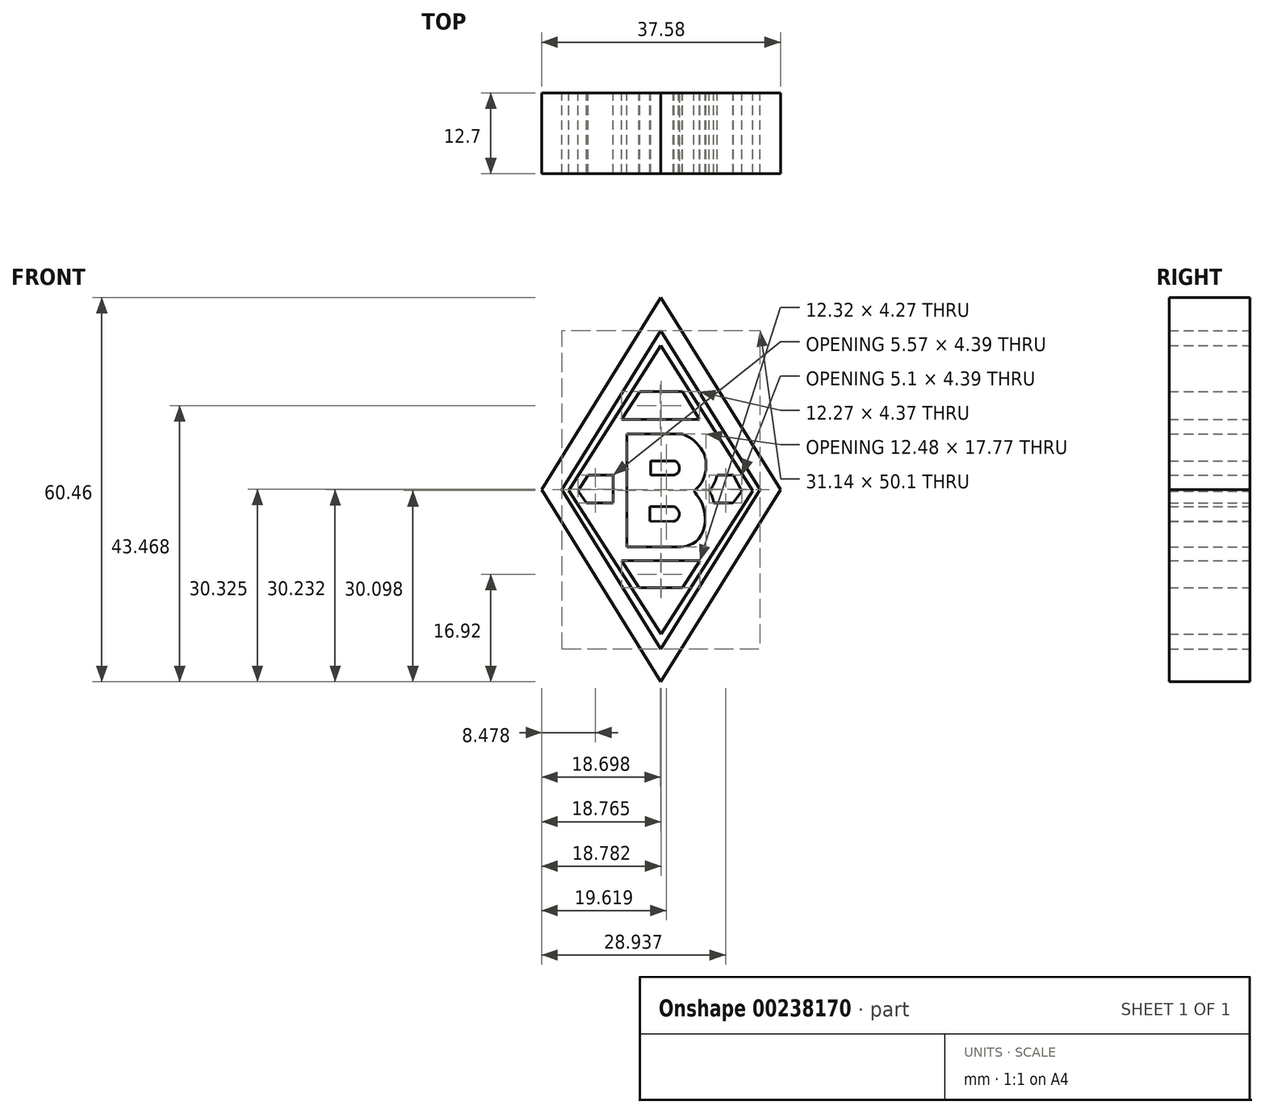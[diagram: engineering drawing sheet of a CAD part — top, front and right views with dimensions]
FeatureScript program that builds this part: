
annotation { "Feature Type Name" : "Feature", "Feature Type Description" : "" }
export const myFeature = defineFeature(function(context is Context, id is Id, definition is map)
    precondition{}
    {
        {
            var Q0;
            Q0=qCreatedBy(makeId("Front.planeOp"),FACE);
            var sketch = newSketch(context, id + "F0", { "sketchPlane" : qUnion([Q0])});
            skLineSegment(sketch, "E0", {"start": v(36.95, 66.96) * mm, "end": v(18.2, 36.72) * mm});
            skPoint(sketch, "E0.startSnap0", {"position": v(36.95, 69.13) * mm});
            skPoint(sketch, "E0.endSnap0", {"position": v(17, 36.72) * mm});
            skLineSegment(sketch, "E1", {"start": v(18.2, 36.72) * mm, "end": v(36.95, 6.5) * mm});
            skPoint(sketch, "E1.endSnap0", {"position": v(36.95, 4.31) * mm});
            skLineSegment(sketch, "E2", {"start": v(36.95, 6.5) * mm, "end": v(55.8, 36.72) * mm});
            skLineSegment(sketch, "E3", {"start": v(55.8, 36.72) * mm, "end": v(36.95, 66.96) * mm});
            skLineSegment(sketch, "E4", {"start": v(21.42, 36.72) * mm, "end": v(36.95, 61.78) * mm});
            skLineSegment(sketch, "E5", {"start": v(36.95, 61.78) * mm, "end": v(52.56, 36.72) * mm});
            skLineSegment(sketch, "E6", {"start": v(52.56, 36.72) * mm, "end": v(36.95, 11.68) * mm});
            skLineSegment(sketch, "E7", {"start": v(36.95, 11.68) * mm, "end": v(21.42, 36.72) * mm});
            skLineSegment(sketch, "E8", {"start": v(22.47, 36.61) * mm, "end": v(36.96, 59.41) * mm});
            skLineSegment(sketch, "E9", {"start": v(36.96, 59.41) * mm, "end": v(51.41, 36.53) * mm});
            skLineSegment(sketch, "E10", {"start": v(51.41, 36.53) * mm, "end": v(37, 14.02) * mm});
            skLineSegment(sketch, "E11", {"start": v(37, 14.02) * mm, "end": v(22.47, 36.61) * mm});
            skLineSegment(sketch, "E12", {"start": v(33.5, 21.29) * mm, "end": v(40.4, 21.29) * mm});
            skLineSegment(sketch, "E13", {"start": v(40.4, 21.29) * mm, "end": v(43.14, 25.55) * mm});
            skLineSegment(sketch, "E14", {"start": v(43.14, 25.55) * mm, "end": v(30.81, 25.55) * mm});
            skLineSegment(sketch, "E15", {"start": v(30.81, 25.55) * mm, "end": v(33.5, 21.29) * mm});
            skLineSegment(sketch, "E16", {"start": v(25.24, 34.63) * mm, "end": v(29.47, 34.63) * mm});
            skLineSegment(sketch, "E17", {"start": v(29.47, 34.63) * mm, "end": v(29.47, 39.02) * mm});
            skLineSegment(sketch, "E18", {"start": v(29.47, 39.02) * mm, "end": v(25.5, 39.02) * mm});
            skLineSegment(sketch, "E19", {"start": v(25.5, 39.02) * mm, "end": v(23.9, 36.53) * mm});
            skLineSegment(sketch, "E20", {"start": v(23.9, 36.53) * mm, "end": v(25.24, 34.63) * mm});
            skLineSegment(sketch, "E21", {"start": v(45.3, 34.63) * mm, "end": v(48.34, 34.63) * mm});
            skLineSegment(sketch, "E22", {"start": v(48.34, 34.63) * mm, "end": v(49.7, 36.47) * mm});
            skLineSegment(sketch, "E23", {"start": v(49.7, 36.47) * mm, "end": v(48.39, 39.02) * mm});
            skLineSegment(sketch, "E24", {"start": v(48.39, 39.02) * mm, "end": v(45.81, 39.02) * mm});
            skFitSpline(sketch, "E25", {"points": [v(45.81, 39.02) * mm, v(45.65, 38.44) * mm, v(45.39, 37.74) * mm, v(44.78, 36.8) * mm, v(44.6, 36.54) * mm], "startDerivative": vector(-0.66, -2.46) * mm, "endDerivative": vector(-0.82, -1.27) * mm});
            skFitSpline(sketch, "E26", {"points": [v(45.3, 34.63) * mm, v(45.12, 35.4) * mm, v(44.8, 36.16) * mm, v(44.6, 36.54) * mm], "startDerivative": vector(-0.39, 2.08) * mm, "endDerivative": vector(-0.7, 1.27) * mm});
            skLineSegment(sketch, "E27", {"start": v(30.77, 47.78) * mm, "end": v(43.04, 47.78) * mm});
            skLineSegment(sketch, "E28", {"start": v(43.04, 47.78) * mm, "end": v(40.4, 52.15) * mm});
            skLineSegment(sketch, "E29", {"start": v(40.4, 52.15) * mm, "end": v(33.63, 52.15) * mm});
            skLineSegment(sketch, "E30", {"start": v(33.63, 52.15) * mm, "end": v(30.77, 47.78) * mm});
            skLineSegment(sketch, "E31", {"start": v(30.58, 46.26) * mm, "end": v(30.58, 26.77) * mm});
            skLineSegment(sketch, "E32", {"start": v(30.58, 26.77) * mm, "end": v(40.4, 26.77) * mm});
            skLineSegment(sketch, "E33", {"start": v(30.58, 46.26) * mm, "end": v(40.42, 46.26) * mm});
            skLineSegment(sketch, "E34", {"start": v(35.34, 39) * mm, "end": v(35.34, 41.26) * mm});
            skLineSegment(sketch, "E35", {"start": v(35.34, 41.26) * mm, "end": v(39, 41.26) * mm});
            skLineSegment(sketch, "E36", {"start": v(35.34, 39) * mm, "end": v(39.04, 39) * mm});
            skLineSegment(sketch, "E37", {"start": v(40.31, 45.48) * mm, "end": v(31.59, 45.48) * mm});
            skLineSegment(sketch, "E38", {"start": v(31.59, 45.48) * mm, "end": v(31.59, 27.71) * mm});
            skLineSegment(sketch, "E39", {"start": v(31.59, 27.71) * mm, "end": v(39.76, 27.71) * mm});
            skLineSegment(sketch, "E40", {"start": v(35.26, 31.77) * mm, "end": v(35.26, 34.09) * mm});
            skLineSegment(sketch, "E41", {"start": v(35.26, 34.09) * mm, "end": v(38.97, 34.09) * mm});
            skLineSegment(sketch, "E42", {"start": v(38.92, 31.73) * mm, "end": v(35.26, 31.77) * mm});
            skFitSpline(sketch, "E43", {"points": [v(39, 41.26) * mm, v(39.28, 41.19) * mm, v(39.66, 40.85) * mm, v(39.87, 40.36) * mm, v(39.89, 39.97) * mm, v(39.8, 39.6) * mm, v(39.52, 39.25) * mm, v(39.04, 39) * mm], "startDerivative": vector(2.33, -0.3) * mm, "endDerivative": vector(-3.25, -1.3) * mm});
            skFitSpline(sketch, "E44", {"points": [v(38.92, 31.73) * mm, v(39.15, 31.8) * mm, v(39.58, 32.1) * mm, v(39.78, 32.47) * mm, v(39.84, 32.65) * mm, v(39.85, 33.05) * mm, v(39.72, 33.45) * mm, v(39.45, 33.83) * mm, v(39.16, 34.01) * mm, v(38.97, 34.09) * mm], "startDerivative": vector(2.26, 0.5) * mm, "endDerivative": vector(-2.13, 0.75) * mm});
            skFitSpline(sketch, "E45", {"points": [v(40.31, 45.48) * mm, v(41, 45.21) * mm, v(42.04, 44.53) * mm, v(43.04, 43.54) * mm, v(43.82, 42.21) * mm, v(44.07, 40.86) * mm, v(44, 39.58) * mm, v(43.53, 38.14) * mm, v(42.65, 36.99) * mm, v(42.18, 36.56) * mm], "startDerivative": vector(7.68, -2.54) * mm, "endDerivative": vector(-5.44, -4.56) * mm});
            skFitSpline(sketch, "E46", {"points": [v(42.18, 36.56) * mm, v(42.65, 35.86) * mm, v(43.33, 34.8) * mm, v(43.69, 33.86) * mm, v(43.9, 32.57) * mm, v(43.82, 31.08) * mm, v(43.13, 29.28) * mm, v(41.75, 28.13) * mm, v(40.58, 27.8) * mm, v(39.76, 27.71) * mm], "startDerivative": vector(4.86, -7.23) * mm, "endDerivative": vector(-8.85, -0.62) * mm});
            skSolve(sketch);
        }
        {
            var Q0;
            Q0 = qSketchRegion(id + "F0", true);
            var Q1;
            Q1=makeQuery(id+"F0.imprint","IMPRINT",FACE,{"disambiguationData":[TD([[makeQuery(id+"F0.imprint","IMPRINT",EDGE,{"derivedFrom":sQuery(id+"F0.wireOp",EDGE,"E8")}),-1.0]])]});
            var Q2;
            Q2=makeQuery(id+"F0.imprint","IMPRINT",FACE,{"disambiguationData":[TD([[makeQuery(id+"F0.imprint","IMPRINT",EDGE,{"derivedFrom":sQuery(id+"F0.wireOp",EDGE,"E40")}),-1.0]])]});
            var Q3;
            Q3=makeQuery(id+"F0.imprint","IMPRINT",FACE,{"disambiguationData":[TD([[makeQuery(id+"F0.imprint","IMPRINT",EDGE,{"derivedFrom":sQuery(id+"F0.wireOp",EDGE,"E34")}),-1.0]])]});
            extrude(context, id + "F1", {"entities" : qUnion([Q0, Q1, Q2, Q3]), "depth" : 12.7 * mm});
        }
    });
